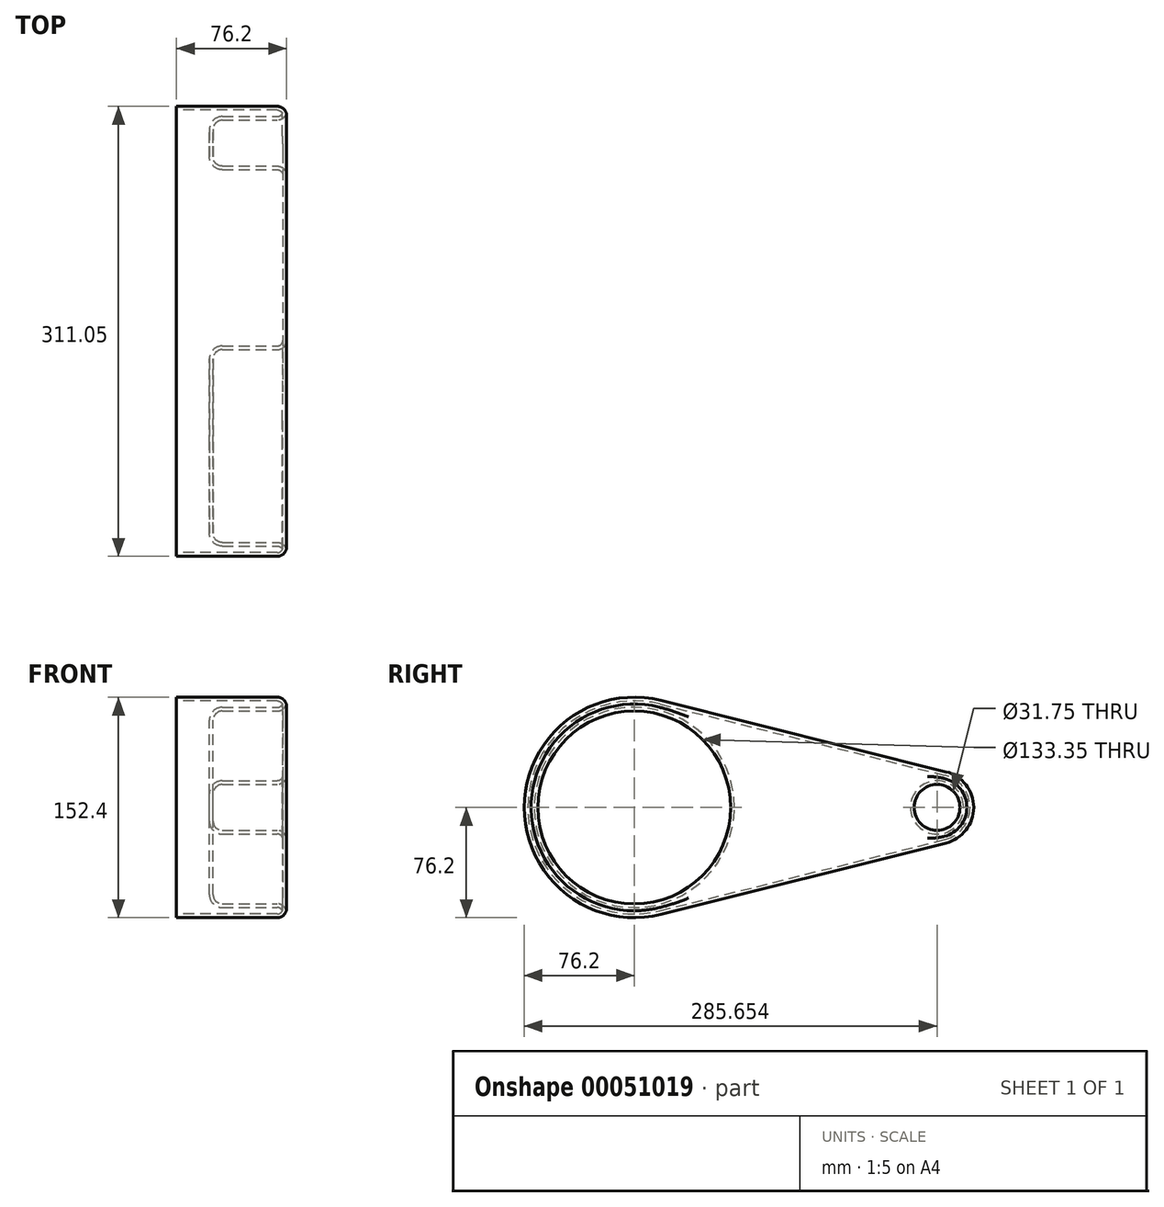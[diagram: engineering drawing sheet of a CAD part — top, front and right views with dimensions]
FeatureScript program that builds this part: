
annotation { "Feature Type Name" : "Feature", "Feature Type Description" : "" }
export const myFeature = defineFeature(function(context is Context, id is Id, definition is map)
    precondition{}
    {
        {
            var Q0;
            Q0=qCreatedBy(makeId("Right.planeOp"),FACE);
            var sketch = newSketch(context, id + "F0", { "sketchPlane" : qUnion([Q0])});
            skCircle(sketch, "E0", {"center": v(0, 0) * mm, "radius": 76.2 * mm});
            skCircle(sketch, "E1", {"center": v(209.45, 0) * mm, "radius": 25.4 * mm});
            skLineSegment(sketch, "E2", {"start": v(18.48, 73.92) * mm, "end": v(215.61, 24.64) * mm});
            skLineSegment(sketch, "E3", {"start": v(18.48, -73.92) * mm, "end": v(215.61, -24.64) * mm});
            skSolve(sketch);
        }
        {
            var Q0;
            Q0 = qSketchRegion(id + "F0", true);
            var Q1;
            {var subQ0=sQuery(id+"F0.wireOp",EDGE,"E0");var subQ1=makeQuery(id+"F0.imprint","INTERSECT",VERTEX,{"derivedFrom":[subQ0,sQuery(id+"F0.wireOp",EDGE,"E2")]});Q1=makeQuery(id+"F0.imprint","IMPRINT",FACE,{"disambiguationData":[TD([[makeQuery(id+"F0.imprint","IMPRINT",EDGE,{"disambiguationData":[TD([[subQ1,-1.0]])],"derivedFrom":subQ0}),1.0]])]});}
            extrude(context, id + "F1", {"entities" : qUnion([Q0, Q1]), "depth" : 76.2 * mm});
        }
        {
            var Q0;
            Q0=makeQuery(id+"F1.opExtrude","CAP_FACE",FACE,{"disambiguationData":[OSD([sQuery(id+"F0.wireOp",EDGE,"E0"),sQuery(id+"F0.wireOp",EDGE,"E1"),sQuery(id+"F0.wireOp",EDGE,"E2"),sQuery(id+"F0.wireOp",EDGE,"E3")])],"isStart":false});
            var sketch = newSketch(context, id + "F2", { "sketchPlane" : qUnion([Q0])});
            skCircle(sketch, "E4", {"center": v(0, 0) * mm, "radius": 66.68 * mm});
            skCircle(sketch, "E5", {"center": v(209.45, 0) * mm, "radius": 15.88 * mm});
            skSolve(sketch);
        }
        {
            var Q0;
            Q0=makeQuery(id+"F2.imprint","IMPRINT",FACE,{"disambiguationData":[TD([[makeQuery(id+"F2.imprint","IMPRINT",EDGE,{"derivedFrom":sQuery(id+"F2.wireOp",EDGE,"E4")}),1.0]])]});
            var Q1;
            Q1=makeQuery(id+"F2.imprint","IMPRINT",FACE,{"disambiguationData":[TD([[makeQuery(id+"F2.imprint","IMPRINT",EDGE,{"derivedFrom":sQuery(id+"F2.wireOp",EDGE,"E5")}),1.0]])]});
            extrude(context, id + "F3", {"entities" : qUnion([Q0, Q1]), "operationType" : NewBodyOperationType.REMOVE, "oppositeDirection" : true, "depth" : 50.8 * mm});
        }
        {
            var Q0;
            Q0=makeQuery(id+"F1.opExtrude","CAP_FACE",FACE,{"disambiguationData":[OSD([sQuery(id+"F0.wireOp",EDGE,"E0"),sQuery(id+"F0.wireOp",EDGE,"E1"),sQuery(id+"F0.wireOp",EDGE,"E2"),sQuery(id+"F0.wireOp",EDGE,"E3")])],"isStart":false});
            var Q1;
            Q1=makeQuery(id+"F3.boolean.opBoolean","COPY",FACE,{"derivedFrom":makeQuery(id+"F3.opExtrude","CAP_FACE",FACE,{"disambiguationData":[OSD([sQuery(id+"F2.wireOp",EDGE,"E4")])],"isStart":false})});
            var Q2;
            Q2=makeQuery(id+"F3.boolean.opBoolean","COPY",FACE,{"derivedFrom":makeQuery(id+"F3.opExtrude","CAP_FACE",FACE,{"disambiguationData":[OSD([sQuery(id+"F2.wireOp",EDGE,"E5")])],"isStart":false})});
            fillet(context, id + "F4", {"entities" : qUnion([Q0, Q1, Q2]), "radius" : 6.35 * mm, "tangentPropagation" : true, "allowEdgeOverflow" : false});
        }
        {
            var Q0;
            Q0=makeQuery(id+"F1.opExtrude","CAP_FACE",FACE,{"disambiguationData":[OSD([sQuery(id+"F0.wireOp",EDGE,"E0"),sQuery(id+"F0.wireOp",EDGE,"E1"),sQuery(id+"F0.wireOp",EDGE,"E2"),sQuery(id+"F0.wireOp",EDGE,"E3")])],"isStart":true});
            shell(context, id + "F5", {"entities" : qUnion([Q0]), "thickness" : 2.54 * mm});
        }
    });
